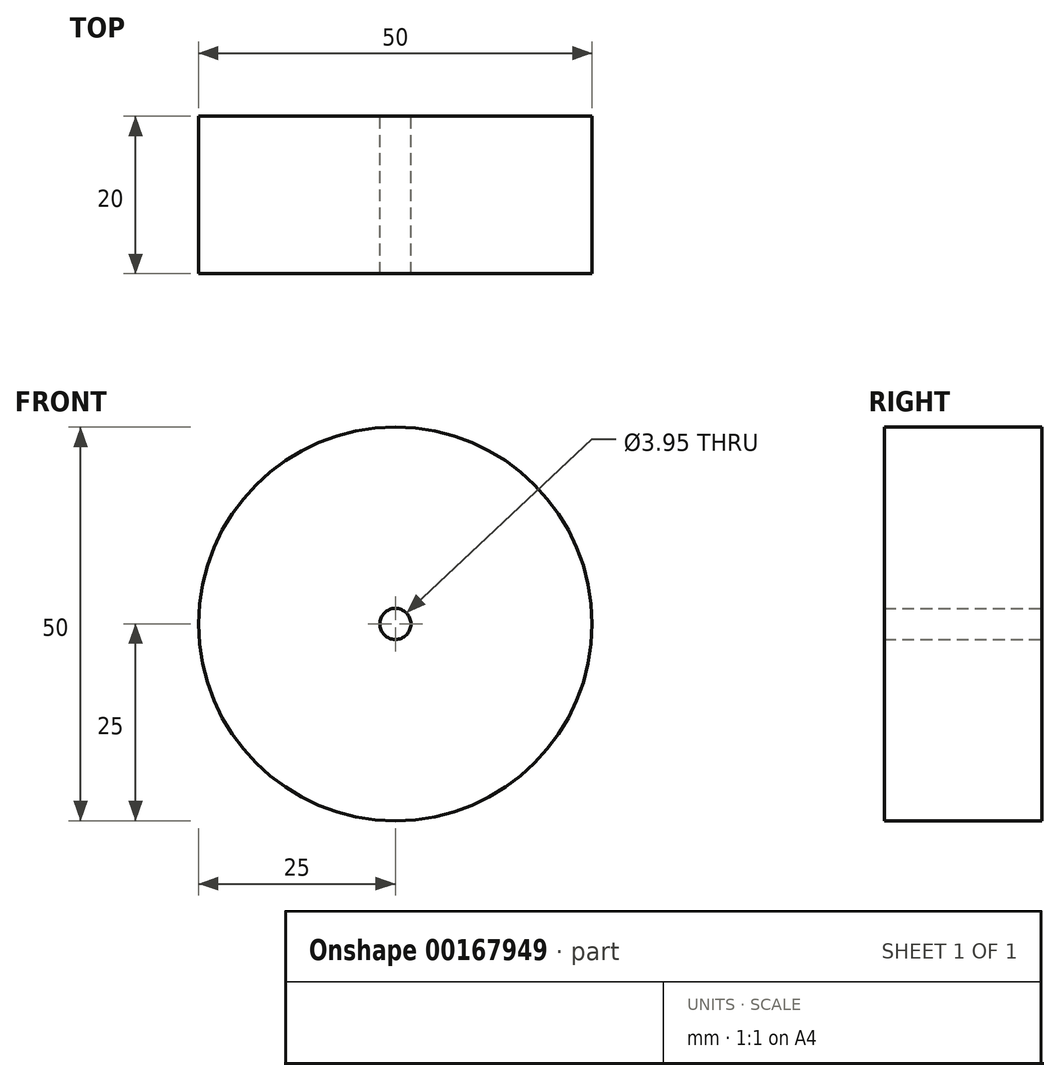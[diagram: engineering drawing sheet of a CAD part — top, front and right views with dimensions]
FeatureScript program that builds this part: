
annotation { "Feature Type Name" : "Feature", "Feature Type Description" : "" }
export const myFeature = defineFeature(function(context is Context, id is Id, definition is map)
    precondition{}
    {
        {
            var Q0;
            Q0=qCreatedBy(makeId("Front.planeOp"),FACE);
            cPlane(context, id + "F0", {"entities" : qUnion([Q0]), "cplaneType" : CPlaneType.OFFSET, "offset" : 0 * mm, "width" : 150 * mm, "height" : 150 * mm});
        }
        {
            var Q0;
            Q0=qCreatedBy(id+"F0.planeOp",FACE);
            var sketch = newSketch(context, id + "F1", { "sketchPlane" : qUnion([Q0])});
            skCircle(sketch, "E0", {"center": v(0, 0) * mm, "radius": 25 * mm});
            skSolve(sketch);
        }
        {
            var Q0;
            Q0 = qSketchRegion(id + "F1", true);
            extrude(context, id + "F2", {"entities" : qUnion([Q0]), "endBound" : BoundingType.SYMMETRIC, "depth" : 20 * mm});
        }
        {
            var Q0;
            Q0=qCreatedBy(makeId("Front.planeOp"),FACE);
            var sketch = newSketch(context, id + "F3", { "sketchPlane" : qUnion([Q0])});
            skCircle(sketch, "E1", {"center": v(0, 0) * mm, "radius": 1.98 * mm});
            skSolve(sketch);
        }
        {
            var Q0;
            Q0 = qSketchRegion(id + "F3", true);
            extrude(context, id + "F4", {"entities" : qUnion([Q0]), "operationType" : NewBodyOperationType.REMOVE, "endBound" : BoundingType.SYMMETRIC, "depth" : 100 * mm});
        }
    });
